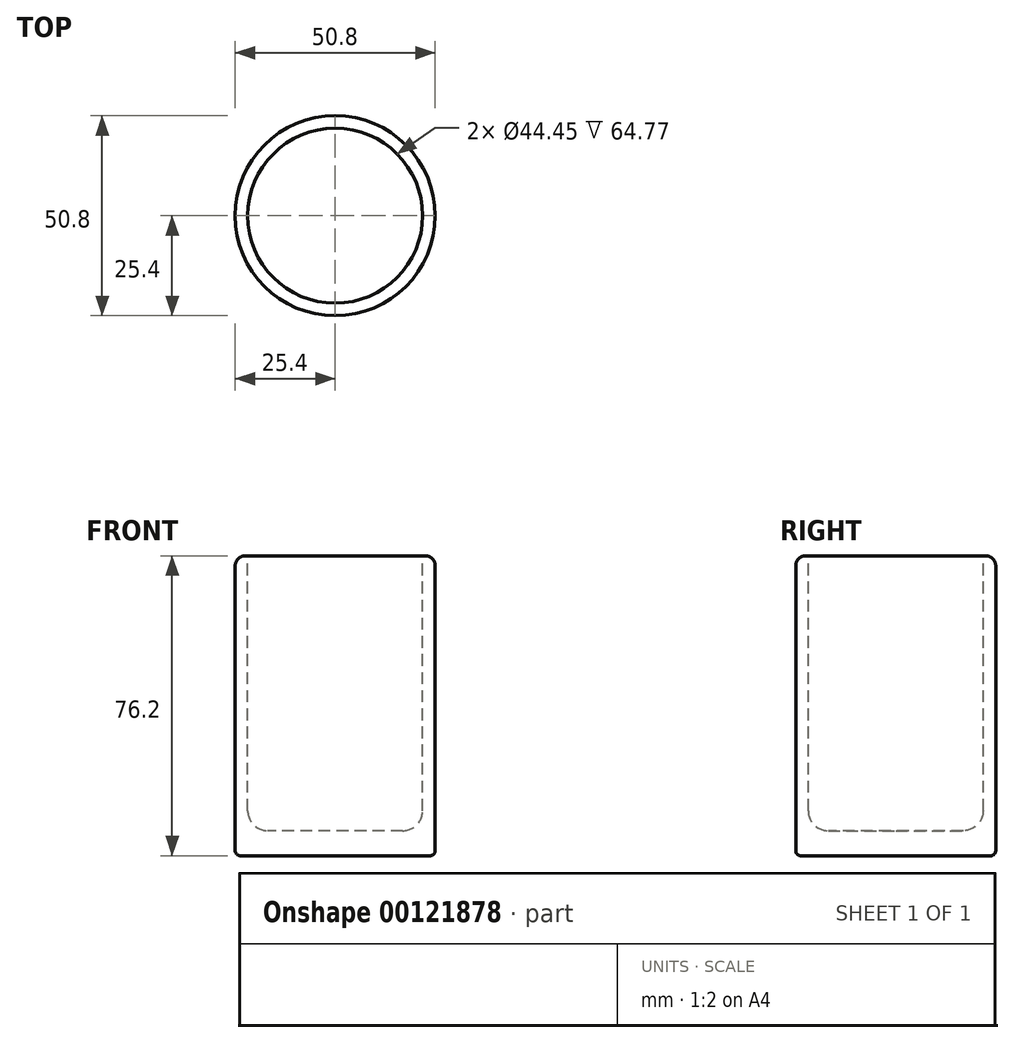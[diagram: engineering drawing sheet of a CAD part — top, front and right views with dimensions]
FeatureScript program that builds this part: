
annotation { "Feature Type Name" : "Feature", "Feature Type Description" : "" }
export const myFeature = defineFeature(function(context is Context, id is Id, definition is map)
    precondition{}
    {
        {
            var Q0;
            Q0=qCreatedBy(makeId("Top.planeOp"),FACE);
            var sketch = newSketch(context, id + "F0", { "sketchPlane" : qUnion([Q0])});
            skCircle(sketch, "E0", {"center": v(0, 0) * mm, "radius": 25.4 * mm});
            skSolve(sketch);
        }
        {
            var Q0;
            Q0=makeQuery(id+"F0.imprint","IMPRINT",FACE,{"disambiguationData":[TD([[makeQuery(id+"F0.imprint","IMPRINT",EDGE,{"derivedFrom":sQuery(id+"F0.wireOp",EDGE,"E0")}),1.0]])]});
            extrude(context, id + "F1", {"entities" : qUnion([Q0]), "depth" : 76.2 * mm});
        }
        {
            var Q0;
            Q0=makeQuery(id+"F1.opExtrude","CAP_FACE",FACE,{"disambiguationData":[OSD([sQuery(id+"F0.wireOp",EDGE,"E0")])],"isStart":false});
            var sketch = newSketch(context, id + "F2", { "sketchPlane" : qUnion([Q0])});
            skCircle(sketch, "E1", {"center": v(0, 0) * mm, "radius": 22.23 * mm});
            skSolve(sketch);
        }
        {
            var Q0;
            Q0=makeQuery(id+"F2.imprint","IMPRINT",FACE,{"disambiguationData":[TD([[makeQuery(id+"F2.imprint","IMPRINT",EDGE,{"derivedFrom":sQuery(id+"F2.wireOp",EDGE,"E1")}),1.0]])]});
            extrude(context, id + "F3", {"entities" : qUnion([Q0]), "operationType" : NewBodyOperationType.REMOVE, "oppositeDirection" : true, "depth" : 69.85 * mm});
        }
        {
            var Q0;
            Q0=makeQuery(id+"F3.boolean.opBoolean","COPY",EDGE,{"derivedFrom":makeQuery(id+"F3.opExtrude","CAP_EDGE",EDGE,{"disambiguationData":[OSD([sQuery(id+"F2.wireOp",EDGE,"E1")])],"isStart":false})});
            fillet(context, id + "F4", {"entities" : qUnion([Q0]), "radius" : 5.08 * mm, "tangentPropagation" : true, "allowEdgeOverflow" : false});
        }
        {
            var Q0;
            Q0=makeQuery(id+"F1.opExtrude","CAP_EDGE",EDGE,{"disambiguationData":[OSD([sQuery(id+"F0.wireOp",EDGE,"E0")])],"isStart":false});
            fillet(context, id + "F5", {"entities" : qUnion([Q0]), "radius" : 2.54 * mm, "tangentPropagation" : true, "allowEdgeOverflow" : false});
        }
        {
            var Q0;
            Q0=makeQuery(id+"F1.opExtrude","CAP_EDGE",EDGE,{"disambiguationData":[OSD([sQuery(id+"F0.wireOp",EDGE,"E0")])],"isStart":true});
            fillet(context, id + "F6", {"entities" : qUnion([Q0]), "radius" : 1.27 * mm, "tangentPropagation" : true, "allowEdgeOverflow" : false});
        }
    });
